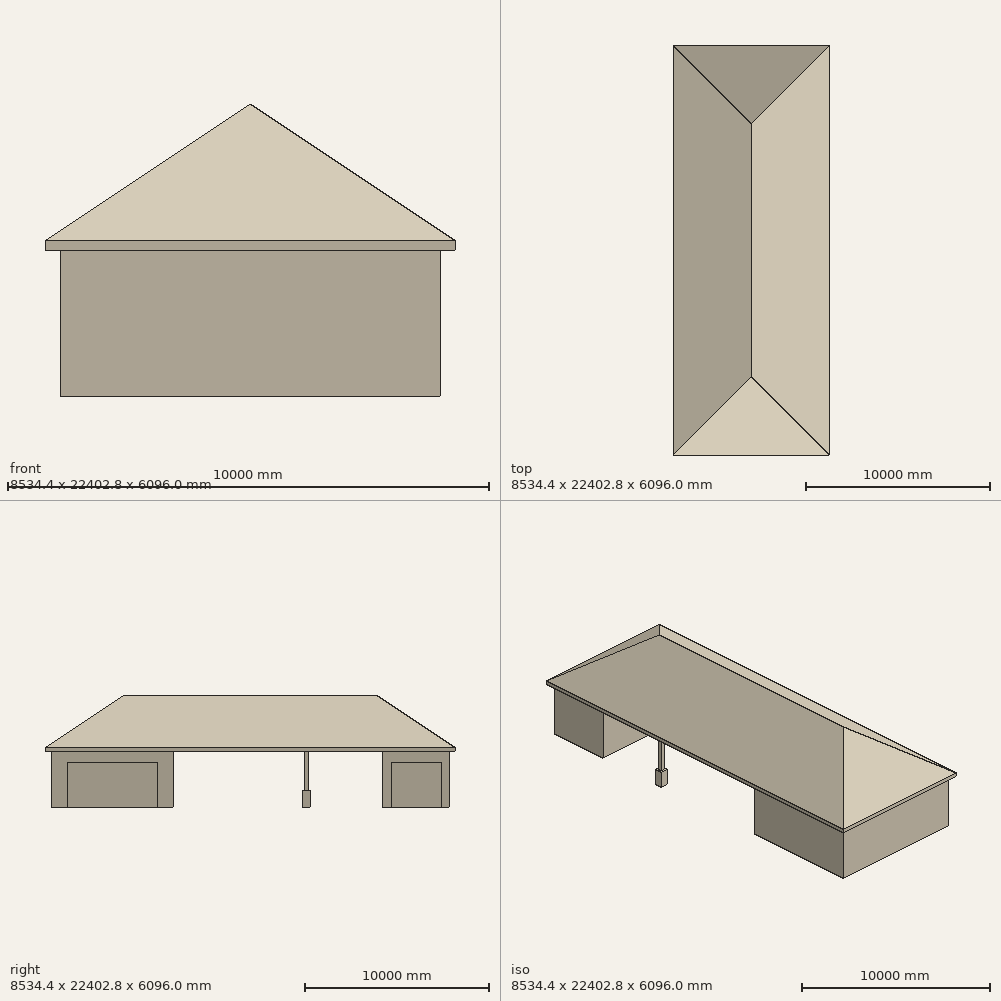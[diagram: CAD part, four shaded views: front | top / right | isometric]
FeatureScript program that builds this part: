
annotation { "Feature Type Name" : "Feature", "Feature Type Description" : "" }
export const myFeature = defineFeature(function(context is Context, id is Id, definition is map)
    precondition{}
    {
        {
            var Q0;
            Q0=qCreatedBy(makeId("Top.planeOp"),FACE);
            var sketch = newSketch(context, id + "F0", { "sketchPlane" : qUnion([Q0])});
            skLineSegment(sketch, "E0.bottom", {"start": v(0, 0) * mm, "end": v(7924.8, 0) * mm});
            skLineSegment(sketch, "E0.top", {"start": v(0, 6705.6) * mm, "end": v(7924.8, 6705.6) * mm});
            skLineSegment(sketch, "E0.left", {"start": v(0, 0) * mm, "end": v(0, 6705.6) * mm});
            skLineSegment(sketch, "E0.right", {"start": v(7924.8, 0) * mm, "end": v(7924.8, 6705.6) * mm});
            skLineSegment(sketch, "E1.bottom", {"start": v(0, 21793.2) * mm, "end": v(7924.8, 21793.2) * mm});
            skLineSegment(sketch, "E1.top", {"start": v(0, 18135.6) * mm, "end": v(7924.8, 18135.6) * mm});
            skLineSegment(sketch, "E1.left", {"start": v(0, 21793.2) * mm, "end": v(0, 18135.6) * mm});
            skLineSegment(sketch, "E1.right", {"start": v(7924.8, 21793.2) * mm, "end": v(7924.8, 18135.6) * mm});
            skLineSegment(sketch, "E2.bottom", {"start": v(0, 14173.2) * mm, "end": v(457.2, 14173.2) * mm});
            skLineSegment(sketch, "E2.top", {"start": v(0, 13716) * mm, "end": v(457.2, 13716) * mm});
            skLineSegment(sketch, "E2.left", {"start": v(0, 14173.2) * mm, "end": v(0, 13716) * mm});
            skLineSegment(sketch, "E2.right", {"start": v(457.2, 14173.2) * mm, "end": v(457.2, 13716) * mm});
            skLineSegment(sketch, "E3.bottom", {"start": v(7924.8, 13716) * mm, "end": v(7467.6, 13716) * mm});
            skLineSegment(sketch, "E3.top", {"start": v(7924.8, 14173.2) * mm, "end": v(7467.6, 14173.2) * mm});
            skLineSegment(sketch, "E3.left", {"start": v(7924.8, 13716) * mm, "end": v(7924.8, 14173.2) * mm});
            skLineSegment(sketch, "E3.right", {"start": v(7467.6, 13716) * mm, "end": v(7467.6, 14173.2) * mm});
            skLineSegment(sketch, "E4.bottom", {"start": v(127, 14046.2) * mm, "end": v(330.2, 14046.2) * mm});
            skLineSegment(sketch, "E4.top", {"start": v(127, 13843) * mm, "end": v(330.2, 13843) * mm});
            skLineSegment(sketch, "E4.left", {"start": v(127, 14046.2) * mm, "end": v(127, 13843) * mm});
            skLineSegment(sketch, "E4.right", {"start": v(330.2, 14046.2) * mm, "end": v(330.2, 13843) * mm});
            skLineSegment(sketch, "E5.bottom", {"start": v(7594.6, 14046.2) * mm, "end": v(7797.8, 14046.2) * mm});
            skLineSegment(sketch, "E5.top", {"start": v(7594.6, 13843) * mm, "end": v(7797.8, 13843) * mm});
            skLineSegment(sketch, "E5.left", {"start": v(7594.6, 14046.2) * mm, "end": v(7594.6, 13843) * mm});
            skLineSegment(sketch, "E5.right", {"start": v(7797.8, 14046.2) * mm, "end": v(7797.8, 13843) * mm});
            skSolve(sketch);
        }
        {
            var Q0;
            Q0=makeQuery(id+"F0.imprint","IMPRINT",FACE,{"disambiguationData":[TD([[makeQuery(id+"F0.imprint","IMPRINT",EDGE,{"derivedFrom":sQuery(id+"F0.wireOp",EDGE,"E0.bottom")}),1.0]])]});
            extrude(context, id + "F1", {"entities" : qUnion([Q0]), "depth" : 3048 * mm, "offsetDistance" : 25.4 * mm});
        }
        {
            var Q0;
            Q0=makeQuery(id+"F1.opExtrude","CAP_FACE",FACE,{"disambiguationData":[OSD([sQuery(id+"F0.wireOp",EDGE,"E0.bottom"),sQuery(id+"F0.wireOp",EDGE,"E0.top"),sQuery(id+"F0.wireOp",EDGE,"E0.left"),sQuery(id+"F0.wireOp",EDGE,"E0.right")])],"isStart":false});
            var sketch = newSketch(context, id + "F2", { "sketchPlane" : qUnion([Q0])});
            skLineSegment(sketch, "E6.bottom", {"start": v(-304.8, 22098) * mm, "end": v(8229.6, 22098) * mm});
            skLineSegment(sketch, "E6.top", {"start": v(-304.8, -304.8) * mm, "end": v(8229.6, -304.8) * mm});
            skLineSegment(sketch, "E6.left", {"start": v(-304.8, 22098) * mm, "end": v(-304.8, -304.8) * mm});
            skLineSegment(sketch, "E6.right", {"start": v(8229.6, 22098) * mm, "end": v(8229.6, -304.8) * mm});
            skSolve(sketch);
        }
        {
            var Q0;
            Q0=qSketchRegion(id+"F2",true);
            extrude(context, id + "F3", {"entities" : qUnion([Q0]), "operationType" : NewBodyOperationType.ADD, "depth" : 6096 * mm, "offsetDistance" : 25.4 * mm});
        }
        {
            var Q0;
            Q0=makeQuery(id+"F3.opExtrude","SWEPT_FACE",FACE,{"disambiguationData":[OSD([sQuery(id+"F2.wireOp",EDGE,"E6.top")])]});
            var sketch = newSketch(context, id + "F4", { "sketchPlane" : qUnion([Q0])});
            skLineSegment(sketch, "E7.0", {"start": v(-304.8, 9144) * mm, "end": v(-304.8, 3048) * mm});
            skLineSegment(sketch, "E8.0", {"start": v(-304.8, 9144) * mm, "end": v(8229.6, 9144) * mm});
            skLineSegment(sketch, "E9.0", {"start": v(8229.6, 9144) * mm, "end": v(8229.6, 3048) * mm});
            skLineSegment(sketch, "E10", {"start": v(-304.8, 3251.2) * mm, "end": v(3962.4, 6096) * mm});
            skLineSegment(sketch, "E11", {"start": v(3962.4, 6096) * mm, "end": v(8229.6, 3251.2) * mm});
            skLineSegment(sketch, "E12", {"start": v(8229.6, 3251.2) * mm, "end": v(7924.8, 3251.2) * mm, "construction": true});
            skLineSegment(sketch, "E13", {"start": v(7924.8, 3251.2) * mm, "end": v(7924.8, 3454.4) * mm, "construction": true});
            skSolve(sketch);
        }
        {
            var Q0;
            Q0=qSketchRegion(id+"F4",true);
            extrude(context, id + "F5", {"entities" : qUnion([Q0]), "operationType" : NewBodyOperationType.REMOVE, "endBound" : BoundingType.THROUGH_ALL, "oppositeDirection" : true, "depth" : 25.4 * mm, "offsetDistance" : 25.4 * mm});
        }
        {
            var Q0;
            Q0=makeQuery(id+"F3.opExtrude","SWEPT_FACE",FACE,{"disambiguationData":[OSD([sQuery(id+"F2.wireOp",EDGE,"E6.right")])]});
            var sketch = newSketch(context, id + "F6", { "sketchPlane" : qUnion([Q0])});
            skLineSegment(sketch, "E14.0", {"start": v(22098, 6096) * mm, "end": v(17830.8, 6096) * mm});
            skLineSegment(sketch, "E15.0", {"start": v(-304.8, 6096) * mm, "end": v(-304.8, 3251.2) * mm});
            skLineSegment(sketch, "E16.0", {"start": v(22098, 3251.2) * mm, "end": v(22098, 6096) * mm});
            skLineSegment(sketch, "E17", {"start": v(-304.8, 3251.2) * mm, "end": v(3962.4, 6096) * mm});
            skLineSegment(sketch, "E18", {"start": v(22098, 3251.2) * mm, "end": v(17830.8, 6096) * mm});
            skLineSegment(sketch, "E19.trimOffspring", {"start": v(3962.4, 6096) * mm, "end": v(-304.8, 6096) * mm});
            skLineSegment(sketch, "E20", {"start": v(-304.8, 3251.2) * mm, "end": v(0, 3251.2) * mm, "construction": true});
            skLineSegment(sketch, "E21", {"start": v(0, 3251.2) * mm, "end": v(0, 3454.4) * mm, "construction": true});
            skSolve(sketch);
        }
        {
            var Q0;
            Q0=qSketchRegion(id+"F6",true);
            extrude(context, id + "F7", {"entities" : qUnion([Q0]), "operationType" : NewBodyOperationType.REMOVE, "endBound" : BoundingType.THROUGH_ALL, "oppositeDirection" : true, "depth" : 25.4 * mm, "offsetDistance" : 25.4 * mm});
        }
        {
            var Q0;
            Q0=makeQuery(id+"F0.imprint","IMPRINT",FACE,{"disambiguationData":[TD([[makeQuery(id+"F0.imprint","IMPRINT",EDGE,{"derivedFrom":sQuery(id+"F0.wireOp",EDGE,"E1.bottom")}),-1.0]])]});
            var Q1;
            Q1=makeQuery(id+"F0.imprint","IMPRINT",FACE,{"disambiguationData":[TD([[makeQuery(id+"F0.imprint","IMPRINT",EDGE,{"derivedFrom":sQuery(id+"F0.wireOp",EDGE,"E5.bottom")}),-1.0]])]});
            var Q2;
            Q2=makeQuery(id+"F0.imprint","IMPRINT",FACE,{"disambiguationData":[TD([[makeQuery(id+"F0.imprint","IMPRINT",EDGE,{"derivedFrom":sQuery(id+"F0.wireOp",EDGE,"E4.bottom")}),-1.0]])]});
            var Q3;
            Q3=makeQuery(id+"F3.opExtrude","CAP_FACE",FACE,{"disambiguationData":[OSD([sQuery(id+"F2.wireOp",EDGE,"E6.bottom"),sQuery(id+"F2.wireOp",EDGE,"E6.top"),sQuery(id+"F2.wireOp",EDGE,"E6.left"),sQuery(id+"F2.wireOp",EDGE,"E6.right")])],"isStart":true});
            var Q4;
            Q4=makeQuery(id+"F1.opExtrude","SWEPT_BODY",BODY,{"disambiguationData":[OSD([sQuery(id+"F0.wireOp",EDGE,"E0.bottom"),sQuery(id+"F0.wireOp",EDGE,"E0.top"),sQuery(id+"F0.wireOp",EDGE,"E0.left"),sQuery(id+"F0.wireOp",EDGE,"E0.right")])]});
            extrude(context, id + "F8", {"entities" : qUnion([Q0, Q1, Q2]), "operationType" : NewBodyOperationType.ADD, "endBound" : BoundingType.UP_TO_SURFACE, "depth" : 25.4 * mm, "endBoundEntityFace" : qUnion([Q3]), "endBoundEntityBody" : qUnion([Q4]), "offsetDistance" : 25.4 * mm});
        }
        {
            var Q0;
            Q0=makeQuery(id+"F0.imprint","IMPRINT",FACE,{"disambiguationData":[TD([[makeQuery(id+"F0.imprint","IMPRINT",EDGE,{"derivedFrom":sQuery(id+"F0.wireOp",EDGE,"E3.bottom")}),-1.0]])]});
            var Q1;
            Q1=makeQuery(id+"F0.imprint","IMPRINT",FACE,{"disambiguationData":[TD([[makeQuery(id+"F0.imprint","IMPRINT",EDGE,{"derivedFrom":sQuery(id+"F0.wireOp",EDGE,"E2.bottom")}),-1.0]])]});
            extrude(context, id + "F9", {"entities" : qUnion([Q0, Q1]), "operationType" : NewBodyOperationType.ADD, "depth" : 914.4 * mm, "offsetDistance" : 25.4 * mm});
        }
        {
            var Q0;
            Q0=makeQuery(id+"F1.opExtrude","SWEPT_FACE",FACE,{"disambiguationData":[OSD([sQuery(id+"F0.wireOp",EDGE,"E0.right")])]});
            var sketch = newSketch(context, id + "F10", { "sketchPlane" : qUnion([Q0])});
            skLineSegment(sketch, "E22.bottom", {"start": v(914.4, 0) * mm, "end": v(5791.2, 0) * mm});
            skLineSegment(sketch, "E22.top", {"start": v(914.4, 2438.4) * mm, "end": v(5791.2, 2438.4) * mm});
            skLineSegment(sketch, "E22.left", {"start": v(914.4, 0) * mm, "end": v(914.4, 2438.4) * mm});
            skLineSegment(sketch, "E22.right", {"start": v(5791.2, 0) * mm, "end": v(5791.2, 2438.4) * mm});
            skLineSegment(sketch, "E23", {"start": v(914.4, 0) * mm, "end": v(0, 0) * mm, "construction": true});
            skLineSegment(sketch, "E24", {"start": v(5791.2, 0) * mm, "end": v(6705.6, 0) * mm, "construction": true});
            skLineSegment(sketch, "E25.bottom", {"start": v(18592.8, 2438.4) * mm, "end": v(21336, 2438.4) * mm});
            skLineSegment(sketch, "E25.top", {"start": v(18592.8, 0) * mm, "end": v(21336, 0) * mm});
            skLineSegment(sketch, "E25.left", {"start": v(18592.8, 2438.4) * mm, "end": v(18592.8, 0) * mm});
            skLineSegment(sketch, "E25.right", {"start": v(21336, 2438.4) * mm, "end": v(21336, 0) * mm});
            skLineSegment(sketch, "E26", {"start": v(18592.8, 0) * mm, "end": v(18135.6, 0) * mm, "construction": true});
            skLineSegment(sketch, "E27", {"start": v(21336, 0) * mm, "end": v(21793.2, 0) * mm, "construction": true});
            skSolve(sketch);
        }
        {
            var Q0;
            Q0=makeQuery(id+"F10.imprint","IMPRINT",FACE,{"disambiguationData":[TD([[makeQuery(id+"F10.imprint","IMPRINT",EDGE,{"derivedFrom":sQuery(id+"F10.wireOp",EDGE,"E22.bottom")}),1.0]])]});
            var Q1;
            Q1=makeQuery(id+"F10.imprint","IMPRINT",FACE,{"disambiguationData":[TD([[makeQuery(id+"F10.imprint","IMPRINT",EDGE,{"derivedFrom":sQuery(id+"F10.wireOp",EDGE,"E25.bottom")}),-1.0]])]});
            extrude(context, id + "F11", {"entities" : qUnion([Q0, Q1]), "operationType" : NewBodyOperationType.REMOVE, "oppositeDirection" : true, "depth" : 76.2 * mm, "offsetDistance" : 25.4 * mm});
        }
        {
            var Q0;
            Q0=makeQuery(id+"F8.opExtrude","SWEPT_FACE",FACE,{"disambiguationData":[OSD([sQuery(id+"F0.wireOp",EDGE,"E1.bottom")])]});
            var sketch = newSketch(context, id + "F12", { "sketchPlane" : qUnion([Q0])});
            skLineSegment(sketch, "E28.bottom", {"start": v(-2743.2, 0) * mm, "end": v(-914.4, 0) * mm});
            skLineSegment(sketch, "E28.top", {"start": v(-2743.2, 2133.6) * mm, "end": v(-914.4, 2133.6) * mm});
            skLineSegment(sketch, "E28.left", {"start": v(-2743.2, 0) * mm, "end": v(-2743.2, 2133.6) * mm});
            skLineSegment(sketch, "E28.right", {"start": v(-914.4, 0) * mm, "end": v(-914.4, 2133.6) * mm});
            skLineSegment(sketch, "E29.bottom", {"start": v(-3352.8, 0) * mm, "end": v(-5181.6, 0) * mm});
            skLineSegment(sketch, "E29.top", {"start": v(-3352.8, 2133.6) * mm, "end": v(-5181.6, 2133.6) * mm});
            skLineSegment(sketch, "E29.left", {"start": v(-3352.8, 0) * mm, "end": v(-3352.8, 2133.6) * mm});
            skLineSegment(sketch, "E29.right", {"start": v(-5181.6, 0) * mm, "end": v(-5181.6, 2133.6) * mm});
            skSolve(sketch);
        }
        {
            var Q0;
            Q0=makeQuery(id+"F12.imprint","IMPRINT",FACE,{"disambiguationData":[TD([[makeQuery(id+"F12.imprint","IMPRINT",EDGE,{"derivedFrom":sQuery(id+"F12.wireOp",EDGE,"E29.bottom")}),-1.0]])]});
            var Q1;
            Q1=makeQuery(id+"F12.imprint","IMPRINT",FACE,{"disambiguationData":[TD([[makeQuery(id+"F12.imprint","IMPRINT",EDGE,{"derivedFrom":sQuery(id+"F12.wireOp",EDGE,"E28.bottom")}),-1.0]])]});
            extrude(context, id + "F13", {"entities" : qUnion([Q0, Q1]), "operationType" : NewBodyOperationType.REMOVE, "oppositeDirection" : true, "depth" : 76.2 * mm, "offsetDistance" : 25.4 * mm});
        }
    });
